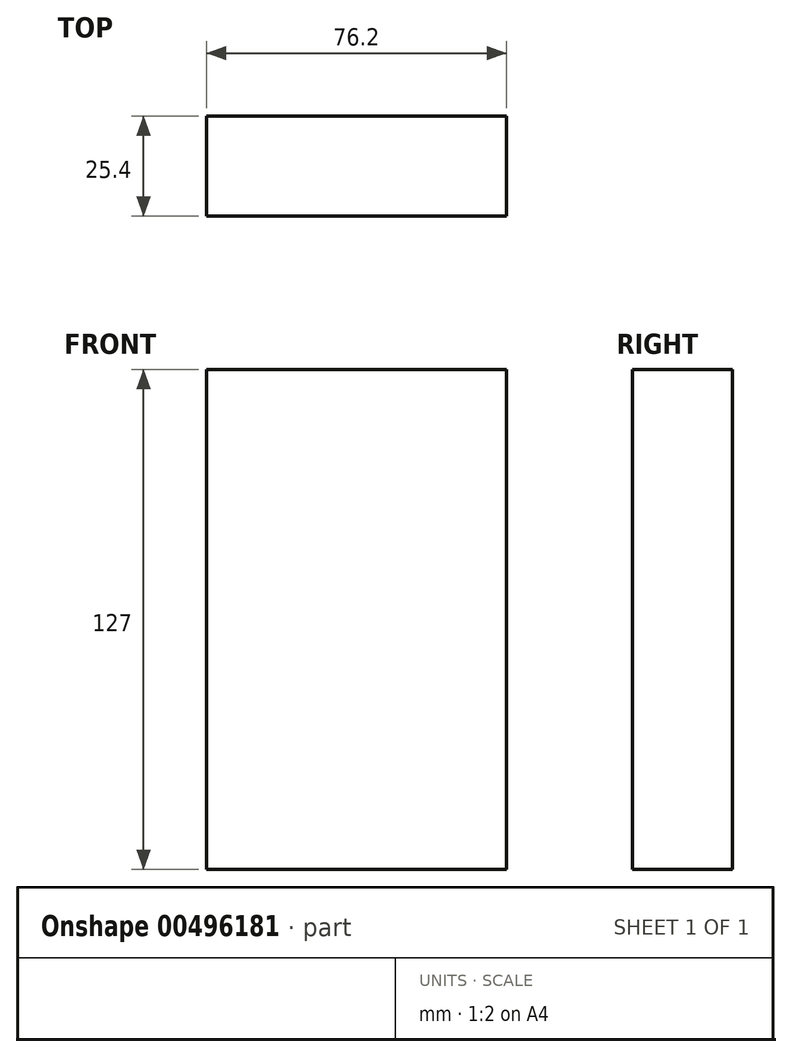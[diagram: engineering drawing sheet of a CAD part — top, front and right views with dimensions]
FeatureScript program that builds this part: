
annotation { "Feature Type Name" : "Feature", "Feature Type Description" : "" }
export const myFeature = defineFeature(function(context is Context, id is Id, definition is map)
    precondition{}
    {
        {
            var Q0;
            Q0=qCreatedBy(makeId("Front.planeOp"),FACE);
            var sketch = newSketch(context, id + "F0", { "sketchPlane" : qUnion([Q0])});
            skLineSegment(sketch, "E0", {"start": v(-30.42, 67.2) * mm, "end": v(-30.42, -59.8) * mm});
            skLineSegment(sketch, "E1", {"start": v(-30.42, -59.8) * mm, "end": v(45.78, -59.8) * mm});
            skLineSegment(sketch, "E2", {"start": v(45.78, -59.8) * mm, "end": v(45.78, 67.2) * mm});
            skLineSegment(sketch, "E3", {"start": v(45.78, 67.2) * mm, "end": v(-30.42, 67.2) * mm});
            skSolve(sketch);
        }
        {
            var Q0;
            Q0=makeQuery(id+"F0.imprint","IMPRINT",FACE,{"disambiguationData":[TD([[makeQuery(id+"F0.imprint","IMPRINT",EDGE,{"derivedFrom":sQuery(id+"F0.wireOp",EDGE,"E0")}),1.0]])]});
            extrude(context, id + "F1", {"entities" : qUnion([Q0]), "depth" : 25.4 * mm});
        }
    });
